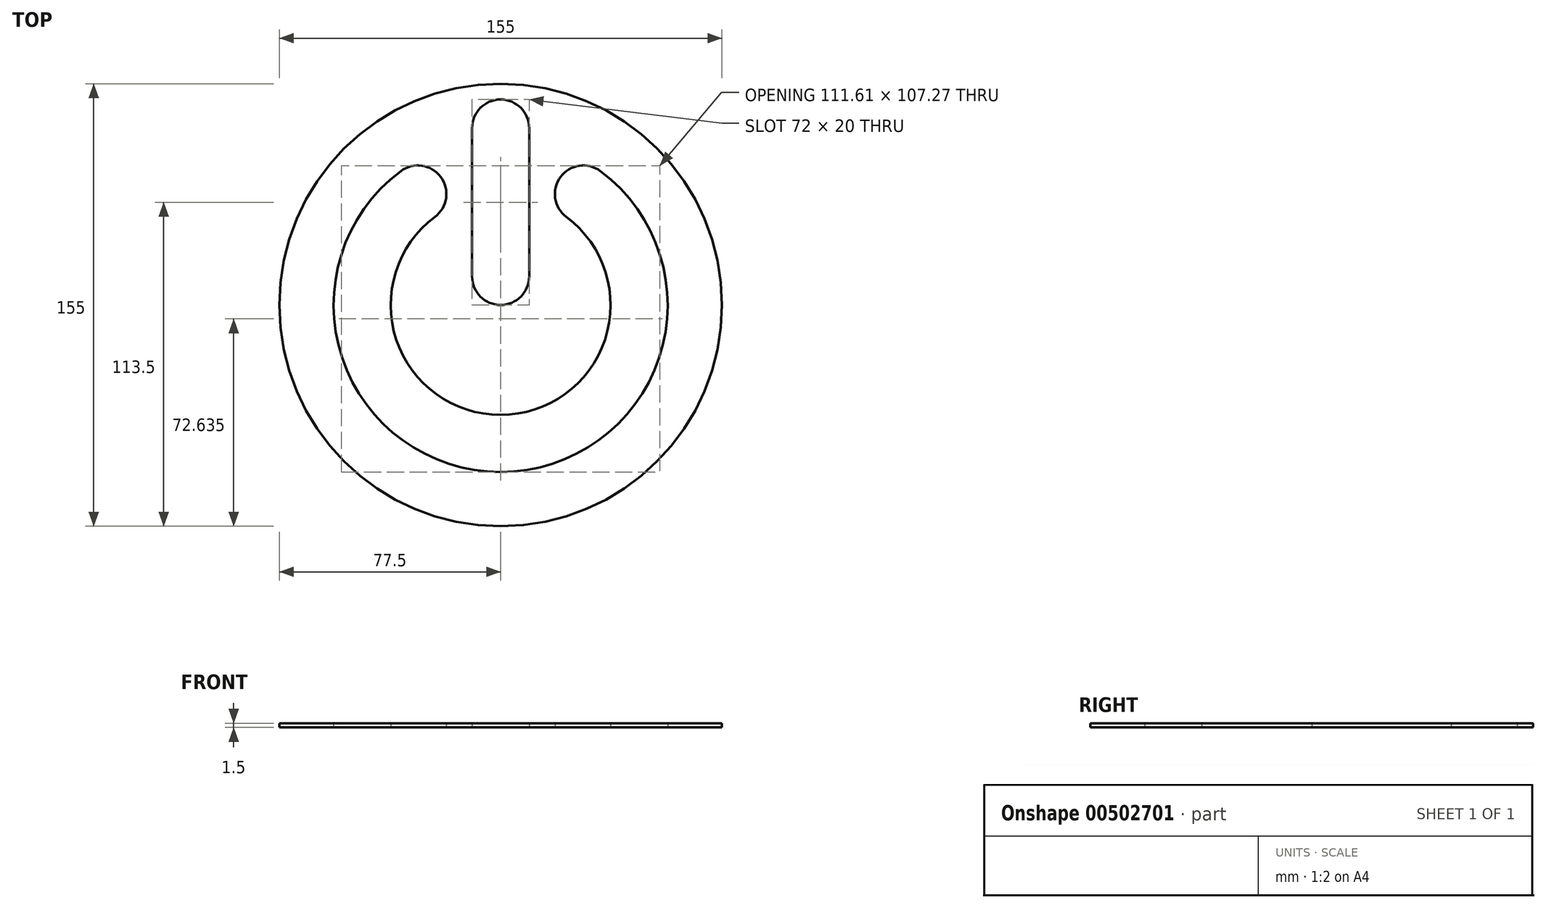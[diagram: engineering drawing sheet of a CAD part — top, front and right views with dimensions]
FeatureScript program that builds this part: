
annotation { "Feature Type Name" : "Feature", "Feature Type Description" : "" }
export const myFeature = defineFeature(function(context is Context, id is Id, definition is map)
    precondition{}
    {
        {
            var Q0;
            Q0=qCreatedBy(makeId("Top.planeOp"),FACE);
            var sketch = newSketch(context, id + "F0", { "sketchPlane" : qUnion([Q0])});
            skArc(sketch, "E0", {"start": v(-34.98, 46.9) * mm, "mid": v(0, -58.5) * mm, "end": v(34.98, 46.9) * mm});
            skArc(sketch, "E1.0", {"start": v(-23.02, 30.86) * mm, "mid": v(0, -38.5) * mm, "end": v(23.02, 30.86) * mm});
            skLineSegment(sketch, "E2", {"start": v(0, 0) * mm, "end": v(0, 81.78) * mm, "construction": true});
            skLineSegment(sketch, "E3.0", {"start": v(29, 0) * mm, "end": v(29, 81.78) * mm, "construction": true});
            skLineSegment(sketch, "E4.0", {"start": v(-29, 0) * mm, "end": v(-29, 81.78) * mm, "construction": true});
            skCircle(sketch, "E5.0", {"center": v(0, 0) * mm, "radius": 48.5 * mm, "construction": true});
            skArc(sketch, "E6", {"start": v(-23.02, 30.86) * mm, "mid": v(-20.98, 44.85) * mm, "end": v(-34.98, 46.9) * mm});
            skArc(sketch, "E7", {"start": v(34.98, 46.9) * mm, "mid": v(20.98, 44.85) * mm, "end": v(23.02, 30.86) * mm});
            skLineSegment(sketch, "E8.0", {"start": v(10, 10) * mm, "end": v(10, 62) * mm});
            skLineSegment(sketch, "E9.0", {"start": v(-10, 10) * mm, "end": v(-10, 62) * mm});
            skArc(sketch, "E10", {"start": v(10, 62) * mm, "mid": v(0, 72) * mm, "end": v(-10, 62) * mm});
            skArc(sketch, "E11", {"start": v(-10, 10) * mm, "mid": v(0, 0) * mm, "end": v(10, 10) * mm});
            skCircle(sketch, "E12", {"center": v(0, 0) * mm, "radius": 77.5 * mm});
            skSolve(sketch);
        }
        {
            var Q0;
            Q0=makeQuery(id+"F0.imprint","IMPRINT",FACE,{"disambiguationData":[TD([[makeQuery(id+"F0.imprint","IMPRINT",EDGE,{"derivedFrom":sQuery(id+"F0.wireOp",EDGE,"E0")}),-1.0]])]});
            extrude(context, id + "F1", {"entities" : qUnion([Q0]), "depth" : 1.5 * mm});
        }
    });
